# Revit family: 2059369 Lighting Fixture_Sylvania_Ascent 150 II Round_Ceiling Recessed
name_source: partatom
category: Lighting Fixtures
revit_build: Autodesk Revit 2017 (Build: 20190507_1515(x64)
units: mm (PartAtom-declared; Revit-internal decimal feet)

## family parameters
Cut with Voids When Loaded = No
Host = Face
Light Source = Yes
OmniClass Number = 23.80.70.11.17
OmniClass Title = Specialized Lighting by Location or Use
Part Type = Normal
Room Calculation Point = No
Round Connector Dimension = Use Diameter
Shared = No

## types (1)
- ASCENT 150 II 3400 4K DALI
    Accessory Material = Aluminum_Sylvania_Ascent 150 II_White
    Apparent Load = 28 VA
    Assembly Code = D5020200
    CRI (Ra) = >80
    Catalog Number = 2059369 ASCENT 150 II 3400 4K DALI
    Color Filter = 16777215
    Colour consistency (SDCM) = 3 step
    Cutout Diameter = 176 mm  [stored 0.577428 ft]
    Default Elevation = 0 mm  [stored 0 ft]
    Description = A very high efficient round downlight up to 127lm/W Long life >50,000hrs 4,000K and 3,000K CCT and CRI Ra85 IP44 rated for wet areas and bathrooms UGR <19 version for offices to comply with EN12464-1 Wide selection of decorative accessories
    Diameter = 189 mm  [stored 0.620079 ft]
    Diffuser Material = Glass_Sylvania_Ascent 150 II_Clear_4000K
    Dimming Lamp Color Temperature Shift = <None>
    Distribution type = Direct
    Drive Current = 1000mA
    Electrical Protection = Class II
    Emit Shape Visible in Rendering = No
    Emit from Circle Diameter = 151 mm
    Energy Class = A++,A+,A
    Glow Wire Test = 650 °C
    IK Rating = IK02
    IP Rating = IP44
    Inner Diameter = 165 mm
    Inner Radius = 82.5 mm
    Inner Reflector Radius = 63 mm
    Inrush Current (max. quantity per 16A C breaker) = 80
    LOR = 100%
    Lamp = LED
    Lamp Comments = Integrated LED
    Life = 50 000 h
    Light Emit  Diameter = 151 mm
    Manufacturer = Feilo Sylvania
    Model = ASCENT 150 II 3400 4K DALI
    Photometric Web File = 2059369_ASCENT150II34004KDALI-206512.ies
    Product Family = ASCENT 150 II ROUND
    Product Page URL = https://www.sylvania-lighting.com
    Radius = 94.5 mm  [stored 0.310039 ft]
    Recessed Depth = 142 mm
    Reflector Material = Metal_Sylvania_Ascent 150 II_Polished
    Ring Inner Diameter = 168 mm  [stored 0.551181 ft]
    Ring Outer Diameter = 172 mm  [stored 0.564304 ft]
    Tilt Angle = -90°
    URL = https://www.sylvania-lighting.com
    Upper Body Material = Metal_Sylvania_Ascent 150 II_Black
    Upper Body Radius = 80 mm  [stored 0.262467 ft]
    Voltage = 230 V
    Voltage Comments = UNV (Universal Voltage; 220-240 Volt)
    Weight = 2 kg

note: [stored X ft] marks values corroborated as IEEE doubles in the binary element streams (Revit-internal decimal feet)

## geometry (parser evidence)
native form markers: Sweep x3
no freeform markers — native parametric forms only
